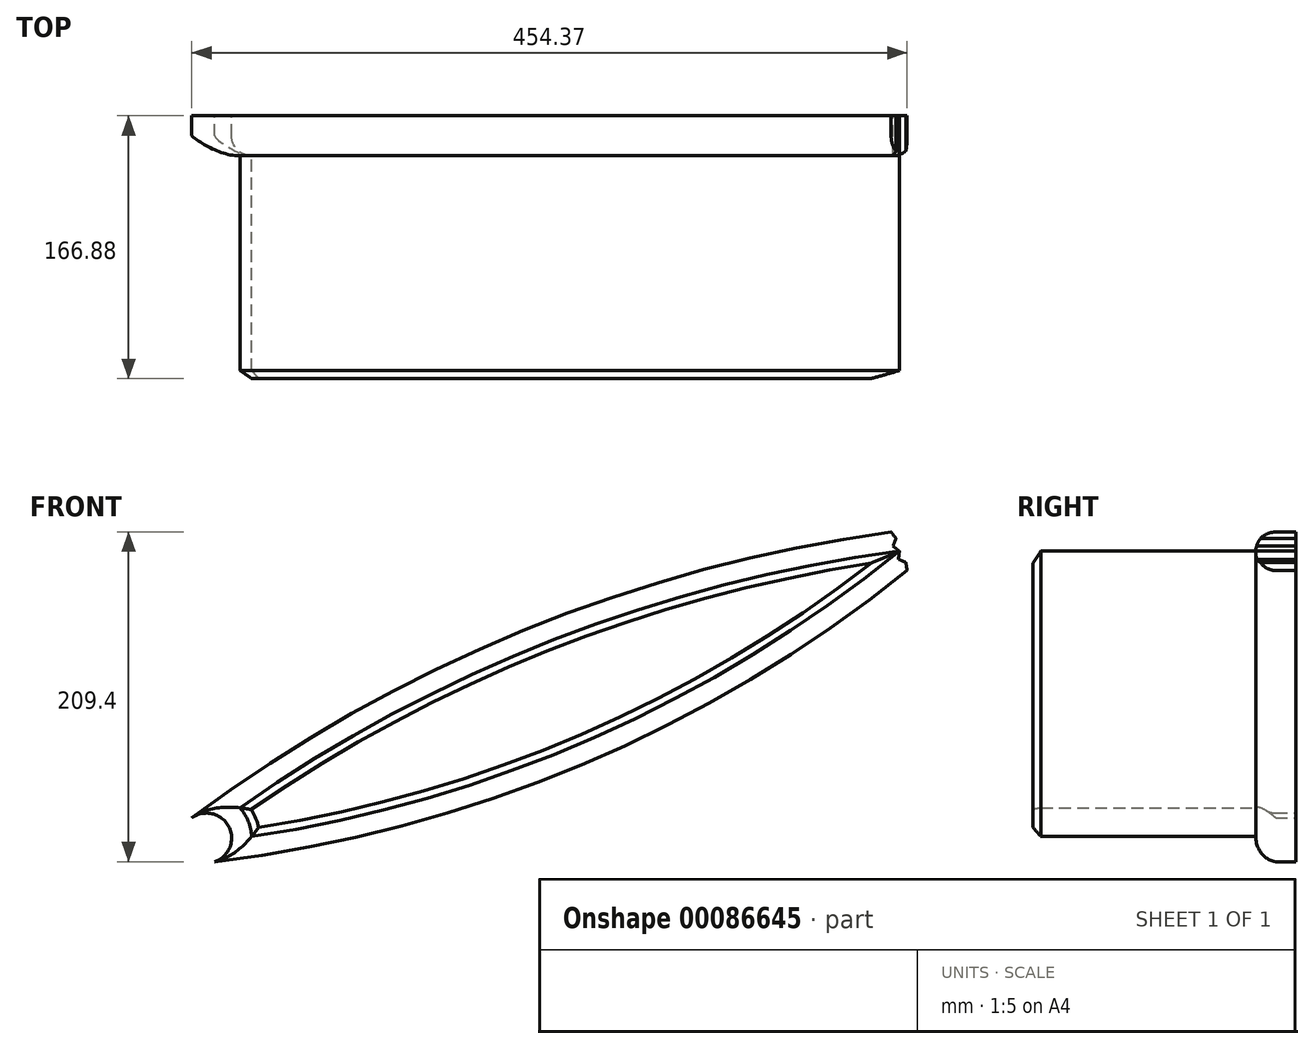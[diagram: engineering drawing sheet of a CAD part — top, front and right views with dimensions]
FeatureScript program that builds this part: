
annotation { "Feature Type Name" : "Feature", "Feature Type Description" : "" }
export const myFeature = defineFeature(function(context is Context, id is Id, definition is map)
    precondition{}
    {
        {
            var Q0;
            Q0=qCreatedBy(makeId("Front.planeOp"),FACE);
            var sketch = newSketch(context, id + "F0", { "sketchPlane" : qUnion([Q0])});
            skLineSegment(sketch, "E0", {"start": v(0, 0) * mm, "end": v(-469.33, -194.4) * mm, "construction": true});
            skLineSegment(sketch, "E1", {"start": v(0, 0) * mm, "end": v(-67.86, 163.83) * mm, "construction": true});
            skCircle(sketch, "E2.cCircle", {"center": v(0, 0) * mm, "radius": 34.3 * mm, "construction": true});
            skLineSegment(sketch, "E2.0", {"start": v(-29.95, -17.3) * mm, "end": v(-33.4, -8.95) * mm, "construction": true});
            skLineSegment(sketch, "E2.1", {"start": v(-33.4, -8.95) * mm, "end": v(-34.59, 0) * mm, "construction": true});
            skLineSegment(sketch, "E2.2", {"start": v(-34.59, 0) * mm, "end": v(-33.4, 8.95) * mm, "construction": true});
            skLineSegment(sketch, "E2.3", {"start": v(-33.4, 8.95) * mm, "end": v(-29.95, 17.3) * mm, "construction": true});
            skLineSegment(sketch, "E2.4", {"start": v(-29.95, 17.3) * mm, "end": v(-24.46, 24.46) * mm, "construction": true});
            skLineSegment(sketch, "E2.5", {"start": v(-24.46, 24.46) * mm, "end": v(-17.3, 29.95) * mm, "construction": true});
            skLineSegment(sketch, "E2.6", {"start": v(-17.3, 29.95) * mm, "end": v(-8.95, 33.4) * mm, "construction": true});
            skLineSegment(sketch, "E2.7", {"start": v(-8.95, 33.4) * mm, "end": v(0, 34.59) * mm, "construction": true});
            skLineSegment(sketch, "E2.8", {"start": v(0, 34.59) * mm, "end": v(8.95, 33.4) * mm, "construction": true});
            skLineSegment(sketch, "E2.9", {"start": v(8.95, 33.4) * mm, "end": v(17.3, 29.95) * mm, "construction": true});
            skLineSegment(sketch, "E2.10", {"start": v(17.3, 29.95) * mm, "end": v(24.46, 24.46) * mm, "construction": true});
            skLineSegment(sketch, "E2.11", {"start": v(24.46, 24.46) * mm, "end": v(29.95, 17.3) * mm, "construction": true});
            skLineSegment(sketch, "E2.12", {"start": v(29.95, 17.3) * mm, "end": v(33.4, 8.95) * mm, "construction": true});
            skLineSegment(sketch, "E2.13", {"start": v(33.4, 8.95) * mm, "end": v(34.59, 0) * mm, "construction": true});
            skLineSegment(sketch, "E2.14", {"start": v(34.59, 0) * mm, "end": v(33.4, -8.95) * mm, "construction": true});
            skLineSegment(sketch, "E2.15", {"start": v(33.4, -8.95) * mm, "end": v(29.95, -17.3) * mm, "construction": true});
            skLineSegment(sketch, "E2.16", {"start": v(29.95, -17.3) * mm, "end": v(24.46, -24.46) * mm, "construction": true});
            skLineSegment(sketch, "E2.17", {"start": v(24.46, -24.46) * mm, "end": v(17.3, -29.95) * mm, "construction": true});
            skLineSegment(sketch, "E2.18", {"start": v(17.3, -29.95) * mm, "end": v(8.95, -33.4) * mm, "construction": true});
            skLineSegment(sketch, "E2.19", {"start": v(8.95, -33.4) * mm, "end": v(0, -34.59) * mm, "construction": true});
            skLineSegment(sketch, "E2.20", {"start": v(0, -34.59) * mm, "end": v(-8.95, -33.4) * mm, "construction": true});
            skLineSegment(sketch, "E2.21", {"start": v(-8.95, -33.4) * mm, "end": v(-17.3, -29.95) * mm, "construction": true});
            skLineSegment(sketch, "E2.22", {"start": v(-17.3, -29.95) * mm, "end": v(-24.46, -24.46) * mm, "construction": true});
            skLineSegment(sketch, "E2.23", {"start": v(-24.46, -24.46) * mm, "end": v(-29.95, -17.3) * mm, "construction": true});
            skPoint(sketch, "E2.0.midPoint", {"position": v(-31.68, -13.12) * mm});
            skCircle(sketch, "E3.cCircle", {"center": v(0, 0) * mm, "radius": 31.75 * mm, "construction": true});
            skLineSegment(sketch, "E3.0", {"start": v(-29.33, -12.15) * mm, "end": v(-31.48, -4.14) * mm, "construction": true});
            skLineSegment(sketch, "E3.1", {"start": v(-31.48, -4.14) * mm, "end": v(-31.48, 4.14) * mm, "construction": true});
            skLineSegment(sketch, "E3.2", {"start": v(-31.48, 4.14) * mm, "end": v(-29.33, 12.15) * mm, "construction": true});
            skLineSegment(sketch, "E3.3", {"start": v(-29.33, 12.15) * mm, "end": v(-25.19, 19.33) * mm, "construction": true});
            skLineSegment(sketch, "E3.4", {"start": v(-25.19, 19.33) * mm, "end": v(-19.33, 25.19) * mm, "construction": true});
            skLineSegment(sketch, "E3.5", {"start": v(-19.33, 25.19) * mm, "end": v(-12.15, 29.33) * mm, "construction": true});
            skLineSegment(sketch, "E3.6", {"start": v(-12.15, 29.33) * mm, "end": v(-4.14, 31.48) * mm, "construction": true});
            skLineSegment(sketch, "E3.7", {"start": v(-4.14, 31.48) * mm, "end": v(4.14, 31.48) * mm, "construction": true});
            skLineSegment(sketch, "E3.8", {"start": v(4.14, 31.48) * mm, "end": v(12.15, 29.33) * mm, "construction": true});
            skLineSegment(sketch, "E3.9", {"start": v(12.15, 29.33) * mm, "end": v(19.33, 25.19) * mm, "construction": true});
            skLineSegment(sketch, "E3.10", {"start": v(19.33, 25.19) * mm, "end": v(25.19, 19.33) * mm, "construction": true});
            skLineSegment(sketch, "E3.11", {"start": v(25.19, 19.33) * mm, "end": v(29.33, 12.15) * mm, "construction": true});
            skLineSegment(sketch, "E3.12", {"start": v(29.33, 12.15) * mm, "end": v(31.48, 4.14) * mm, "construction": true});
            skLineSegment(sketch, "E3.13", {"start": v(31.48, 4.14) * mm, "end": v(31.48, -4.14) * mm, "construction": true});
            skLineSegment(sketch, "E3.14", {"start": v(31.48, -4.14) * mm, "end": v(29.33, -12.15) * mm, "construction": true});
            skLineSegment(sketch, "E3.15", {"start": v(29.33, -12.15) * mm, "end": v(25.19, -19.33) * mm, "construction": true});
            skLineSegment(sketch, "E3.16", {"start": v(25.19, -19.33) * mm, "end": v(19.33, -25.19) * mm, "construction": true});
            skLineSegment(sketch, "E3.17", {"start": v(19.33, -25.19) * mm, "end": v(12.15, -29.33) * mm, "construction": true});
            skLineSegment(sketch, "E3.18", {"start": v(12.15, -29.33) * mm, "end": v(4.14, -31.48) * mm, "construction": true});
            skLineSegment(sketch, "E3.19", {"start": v(4.14, -31.48) * mm, "end": v(-4.14, -31.48) * mm, "construction": true});
            skLineSegment(sketch, "E3.20", {"start": v(-4.14, -31.48) * mm, "end": v(-12.15, -29.33) * mm, "construction": true});
            skLineSegment(sketch, "E3.21", {"start": v(-12.15, -29.33) * mm, "end": v(-19.33, -25.19) * mm, "construction": true});
            skLineSegment(sketch, "E3.22", {"start": v(-19.33, -25.19) * mm, "end": v(-25.19, -19.33) * mm, "construction": true});
            skLineSegment(sketch, "E3.23", {"start": v(-25.19, -19.33) * mm, "end": v(-29.33, -12.15) * mm, "construction": true});
            skLineSegment(sketch, "E4", {"start": v(-31.48, 4.14) * mm, "end": v(-33.4, 8.95) * mm});
            skLineSegment(sketch, "E5", {"start": v(-29.33, 12.15) * mm, "end": v(-33.4, 8.95) * mm});
            skLineSegment(sketch, "E6", {"start": v(-29.33, 12.15) * mm, "end": v(-29.95, 17.3) * mm});
            skLineSegment(sketch, "E7", {"start": v(-25.19, 19.33) * mm, "end": v(-29.95, 17.3) * mm});
            skLineSegment(sketch, "E8", {"start": v(-25.19, 19.33) * mm, "end": v(-24.46, 24.46) * mm});
            skLineSegment(sketch, "E9", {"start": v(-19.33, 25.19) * mm, "end": v(-24.46, 24.46) * mm});
            skLineSegment(sketch, "E10", {"start": v(-19.33, 25.19) * mm, "end": v(-17.3, 29.95) * mm});
            skLineSegment(sketch, "E11", {"start": v(-12.15, 29.33) * mm, "end": v(-17.3, 29.95) * mm});
            skLineSegment(sketch, "E12", {"start": v(-12.15, 29.33) * mm, "end": v(-8.95, 33.4) * mm});
            skLineSegment(sketch, "E13", {"start": v(-4.14, 31.48) * mm, "end": v(-8.95, 33.4) * mm});
            skLineSegment(sketch, "E14", {"start": v(-4.14, 31.48) * mm, "end": v(0, 34.59) * mm});
            skLineSegment(sketch, "E15", {"start": v(4.14, 31.48) * mm, "end": v(0, 34.59) * mm});
            skLineSegment(sketch, "E16", {"start": v(4.14, 31.48) * mm, "end": v(8.95, 33.4) * mm});
            skLineSegment(sketch, "E17", {"start": v(12.15, 29.33) * mm, "end": v(8.95, 33.4) * mm});
            skLineSegment(sketch, "E18", {"start": v(12.15, 29.33) * mm, "end": v(17.3, 29.95) * mm});
            skLineSegment(sketch, "E19", {"start": v(19.33, 25.19) * mm, "end": v(17.3, 29.95) * mm});
            skLineSegment(sketch, "E20", {"start": v(24.46, 24.46) * mm, "end": v(19.33, 25.19) * mm});
            skLineSegment(sketch, "E21", {"start": v(25.19, 19.33) * mm, "end": v(24.46, 24.46) * mm});
            skLineSegment(sketch, "E22", {"start": v(29.95, 17.3) * mm, "end": v(25.19, 19.33) * mm});
            skLineSegment(sketch, "E23", {"start": v(29.95, 17.3) * mm, "end": v(29.33, 12.15) * mm});
            skLineSegment(sketch, "E24", {"start": v(29.33, 12.15) * mm, "end": v(33.4, 8.95) * mm});
            skLineSegment(sketch, "E25", {"start": v(33.4, 8.95) * mm, "end": v(31.48, 4.14) * mm});
            skLineSegment(sketch, "E26", {"start": v(31.48, 4.14) * mm, "end": v(34.59, 0) * mm});
            skLineSegment(sketch, "E27", {"start": v(34.59, 0) * mm, "end": v(31.48, -4.14) * mm});
            skLineSegment(sketch, "E28", {"start": v(33.4, -8.95) * mm, "end": v(31.48, -4.14) * mm});
            skLineSegment(sketch, "E29", {"start": v(33.4, -8.95) * mm, "end": v(29.33, -12.15) * mm});
            skLineSegment(sketch, "E30", {"start": v(29.33, -12.15) * mm, "end": v(29.95, -17.3) * mm});
            skLineSegment(sketch, "E31", {"start": v(29.95, -17.3) * mm, "end": v(25.19, -19.33) * mm});
            skLineSegment(sketch, "E32", {"start": v(24.46, -24.46) * mm, "end": v(25.19, -19.33) * mm});
            skLineSegment(sketch, "E33", {"start": v(24.46, -24.46) * mm, "end": v(19.33, -25.19) * mm});
            skLineSegment(sketch, "E34", {"start": v(19.33, -25.19) * mm, "end": v(17.3, -29.95) * mm});
            skLineSegment(sketch, "E35", {"start": v(17.3, -29.95) * mm, "end": v(12.15, -29.33) * mm});
            skLineSegment(sketch, "E36", {"start": v(12.15, -29.33) * mm, "end": v(8.95, -33.4) * mm});
            skLineSegment(sketch, "E37", {"start": v(8.95, -33.4) * mm, "end": v(4.14, -31.48) * mm});
            skLineSegment(sketch, "E38", {"start": v(4.14, -31.48) * mm, "end": v(0, -34.59) * mm});
            skLineSegment(sketch, "E39", {"start": v(0, -34.59) * mm, "end": v(-4.14, -31.48) * mm});
            skLineSegment(sketch, "E40", {"start": v(-4.14, -31.48) * mm, "end": v(-8.95, -33.4) * mm});
            skLineSegment(sketch, "E41", {"start": v(-8.95, -33.4) * mm, "end": v(-12.15, -29.33) * mm});
            skLineSegment(sketch, "E42", {"start": v(-12.15, -29.33) * mm, "end": v(-17.3, -29.95) * mm});
            skLineSegment(sketch, "E43", {"start": v(-17.3, -29.95) * mm, "end": v(-19.33, -25.19) * mm});
            skLineSegment(sketch, "E44", {"start": v(-19.33, -25.19) * mm, "end": v(-24.46, -24.46) * mm});
            skLineSegment(sketch, "E45", {"start": v(-24.46, -24.46) * mm, "end": v(-25.19, -19.33) * mm});
            skLineSegment(sketch, "E46", {"start": v(-25.19, -19.33) * mm, "end": v(-29.95, -17.3) * mm});
            skLineSegment(sketch, "E47", {"start": v(-29.95, -17.3) * mm, "end": v(-29.33, -12.15) * mm});
            skLineSegment(sketch, "E48", {"start": v(-29.33, -12.15) * mm, "end": v(-33.4, -8.95) * mm});
            skLineSegment(sketch, "E49", {"start": v(-33.4, -8.95) * mm, "end": v(-31.48, -4.14) * mm});
            skLineSegment(sketch, "E50", {"start": v(-31.48, -4.14) * mm, "end": v(-34.59, 0) * mm});
            skLineSegment(sketch, "E51", {"start": v(-31.48, 4.14) * mm, "end": v(-34.59, 0) * mm});
            skCircle(sketch, "E52", {"center": v(0, 0) * mm, "radius": 25.4 * mm});
            skCircle(sketch, "E53", {"center": v(-469.33, -194.4) * mm, "radius": 15.88 * mm});
            skArc(sketch, "E54", {"start": v(-34.59, 0) * mm, "mid": v(-268.28, -62.56) * mm, "end": v(-478.83, -181.68) * mm});
            skArc(sketch, "E55", {"start": v(-464.13, -209.4) * mm, "mid": v(-231.28, -147.88) * mm, "end": v(-24.46, -24.46) * mm});
            skSolve(sketch);
        }
        {
            var Q0;
            Q0=makeQuery(id+"F0.imprint","IMPRINT",FACE,{"disambiguationData":[TD([[makeQuery(id+"F0.imprint","IMPRINT",EDGE,{"derivedFrom":sQuery(id+"F0.wireOp",EDGE,"E45")}),1.0]])]});
            extrude(context, id + "F1", {"entities" : qUnion([Q0]), "depth" : 25.4 * mm});
        }
        {
            var Q0;
            Q0=makeQuery(id+"F1.opExtrude","CAP_EDGE",EDGE,{"disambiguationData":[OSD([sQuery(id+"F0.wireOp",EDGE,"E55")])],"isStart":false});
            var Q1;
            Q1=makeQuery(id+"F1.opExtrude","CAP_EDGE",EDGE,{"disambiguationData":[OSD([sQuery(id+"F0.wireOp",EDGE,"E54")])],"isStart":false});
            var Q2;
            Q2=makeQuery(id+"F1.opExtrude","CAP_EDGE",EDGE,{"disambiguationData":[OSD([sQuery(id+"F0.wireOp",EDGE,"E53")])],"isStart":false});
            fillet(context, id + "F2", {"entities" : qUnion([Q0, Q1, Q2]), "radius" : 12.7 * mm, "tangentPropagation" : true, "allowEdgeOverflow" : false});
        }
        {
            var Q0;
            Q0=makeQuery(id+"F1.opExtrude","CAP_FACE",FACE,{"disambiguationData":[OSD([sQuery(id+"F0.wireOp",EDGE,"E45"),sQuery(id+"F0.wireOp",EDGE,"E46"),sQuery(id+"F0.wireOp",EDGE,"E47"),sQuery(id+"F0.wireOp",EDGE,"E48"),sQuery(id+"F0.wireOp",EDGE,"E49"),sQuery(id+"F0.wireOp",EDGE,"E50"),sQuery(id+"F0.wireOp",EDGE,"E53"),sQuery(id+"F0.wireOp",EDGE,"E54"),sQuery(id+"F0.wireOp",EDGE,"E55")])],"isStart":false});
            extrude(context, id + "F3", {"entities" : qUnion([Q0]), "operationType" : NewBodyOperationType.ADD, "depth" : 141.48 * mm});
        }
        {
            var Q0;
            {var subQ0=sQuery(id+"F0.wireOp",EDGE,"E55");var subQ1=sQuery(id+"F0.wireOp",EDGE,"E54");var subQ2=sQuery(id+"F0.wireOp",EDGE,"E53");var subQ3=sQuery(id+"F0.wireOp",EDGE,"E50");var subQ4=sQuery(id+"F0.wireOp",EDGE,"E49");var subQ5=sQuery(id+"F0.wireOp",EDGE,"E48");var subQ6=sQuery(id+"F0.wireOp",EDGE,"E47");var subQ7=sQuery(id+"F0.wireOp",EDGE,"E46");var subQ8=sQuery(id+"F0.wireOp",EDGE,"E45");Q0=makeQuery(id+"F3.opExtrude","CAP_EDGE",EDGE,{"disambiguationData":[OSD([subQ8,subQ7,subQ6,subQ5,subQ4,subQ3,subQ2,subQ1,subQ0]),TDD([makeQuery(id+"F2.opFillet","BLEND_EDGE",EDGE,{"blendedFrom":[makeQuery(id+"F1.opExtrude","CAP_EDGE",EDGE,{"disambiguationData":[OSD([subQ0])],"isStart":false}),makeQuery(id+"F1.opExtrude","CAP_FACE",FACE,{"disambiguationData":[OSD([subQ8,subQ7,subQ6,subQ5,subQ4,subQ3,subQ2,subQ1,subQ0])],"isStart":false})],"blendedInto":[makeQuery(id+"F1.opExtrude","CAP_FACE",FACE,{"disambiguationData":[OSD([subQ8,subQ7,subQ6,subQ5,subQ4,subQ3,subQ2,subQ1,subQ0])],"isStart":false})]})])],"isStart":false});}
            var Q1;
            {var subQ0=sQuery(id+"F0.wireOp",EDGE,"E55");var subQ1=sQuery(id+"F0.wireOp",EDGE,"E54");var subQ2=sQuery(id+"F0.wireOp",EDGE,"E53");var subQ3=sQuery(id+"F0.wireOp",EDGE,"E50");var subQ4=sQuery(id+"F0.wireOp",EDGE,"E49");var subQ5=sQuery(id+"F0.wireOp",EDGE,"E48");var subQ6=sQuery(id+"F0.wireOp",EDGE,"E47");var subQ7=sQuery(id+"F0.wireOp",EDGE,"E46");var subQ8=sQuery(id+"F0.wireOp",EDGE,"E45");Q1=makeQuery(id+"F3.opExtrude","CAP_EDGE",EDGE,{"disambiguationData":[OSD([subQ8,subQ7,subQ6,subQ5,subQ4,subQ3,subQ2,subQ1,subQ0]),TDD([makeQuery(id+"F2.opFillet","BLEND_EDGE",EDGE,{"blendedFrom":[makeQuery(id+"F1.opExtrude","CAP_EDGE",EDGE,{"disambiguationData":[OSD([subQ1])],"isStart":false}),makeQuery(id+"F1.opExtrude","CAP_FACE",FACE,{"disambiguationData":[OSD([subQ8,subQ7,subQ6,subQ5,subQ4,subQ3,subQ2,subQ1,subQ0])],"isStart":false})],"blendedInto":[makeQuery(id+"F1.opExtrude","CAP_FACE",FACE,{"disambiguationData":[OSD([subQ8,subQ7,subQ6,subQ5,subQ4,subQ3,subQ2,subQ1,subQ0])],"isStart":false})]})])],"isStart":false});}
            var Q2;
            {var subQ0=sQuery(id+"F0.wireOp",EDGE,"E55");var subQ1=sQuery(id+"F0.wireOp",EDGE,"E54");var subQ2=sQuery(id+"F0.wireOp",EDGE,"E53");var subQ3=sQuery(id+"F0.wireOp",EDGE,"E50");var subQ4=sQuery(id+"F0.wireOp",EDGE,"E49");var subQ5=sQuery(id+"F0.wireOp",EDGE,"E48");var subQ6=sQuery(id+"F0.wireOp",EDGE,"E47");var subQ7=sQuery(id+"F0.wireOp",EDGE,"E46");var subQ8=sQuery(id+"F0.wireOp",EDGE,"E45");Q2=makeQuery(id+"F3.opExtrude","CAP_EDGE",EDGE,{"disambiguationData":[OSD([subQ8,subQ7,subQ6,subQ5,subQ4,subQ3,subQ2,subQ1,subQ0]),TDD([makeQuery(id+"F2.opFillet","BLEND_EDGE",EDGE,{"blendedFrom":[makeQuery(id+"F1.opExtrude","CAP_EDGE",EDGE,{"disambiguationData":[OSD([subQ2])],"isStart":false}),makeQuery(id+"F1.opExtrude","CAP_FACE",FACE,{"disambiguationData":[OSD([subQ8,subQ7,subQ6,subQ5,subQ4,subQ3,subQ2,subQ1,subQ0])],"isStart":false})],"blendedInto":[makeQuery(id+"F1.opExtrude","CAP_FACE",FACE,{"disambiguationData":[OSD([subQ8,subQ7,subQ6,subQ5,subQ4,subQ3,subQ2,subQ1,subQ0])],"isStart":false})]})])],"isStart":false});}
            chamfer(context, id + "F4", {"entities" : qUnion([Q0, Q1, Q2]), "width" : 5.08 * mm, "tangentPropagation" : true});
        }
    });
